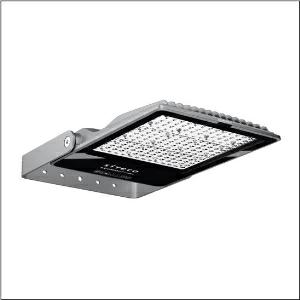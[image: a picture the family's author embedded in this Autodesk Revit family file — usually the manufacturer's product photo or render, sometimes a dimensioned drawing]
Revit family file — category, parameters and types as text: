
# Revit family: sicompact_r__31_midi___pl32_5xa7581d1k23_6975
name_source: partatom
category: Lighting Fixtures
units: mm (PartAtom-declared; Revit-internal decimal feet)

## family parameters
Cut with Voids When Loaded = No
Host = Face
Light Source = No
Part Type = Normal
Room Calculation Point = No
Round Connector Dimension = Use Diameter
Shared = No

## types (1)
- SiCompact® 31 midi  PL32 (1 x LED, 27000 lm, 171 W, 3000K)
    Apparent Load = 171 VA
    CIE Flux Codes = 32 69 98 100 100
    Color Rendering = 70
    Color Temperature = 3000K
    Default Elevation = 1800 mm
    Description = SiCompact® 31 midi, floodlight, primary light control with lens, of plastic, of toughened safety glass, transparent, light distribution: PL32, light emission: direct distribution, primary light characteristic: asymmetric, installation type: surface-mounted, LED, High Power LED, rated luminous flux: 27.000lm, luminous efficacy: 158lm/W, light colour: 730, colour temperature: 3000K, control gear: ECG, with cable, 3x 1.5mm², mains connection: 220..240V, AC, 50/60Hz, connection cable pre-assembled, cable length: 2m, rated input power: 171W, of diecast aluminium, specular, metallic grey (RAL 9006), length: 560mm, width: 330mm, height: 62mm, bracket, of sheet steel, coated, metallic grey (RAL 9006), ON/OFF, protection rating (complete): IP66, insulation class (complete): insulation class I (protective earthing), certification: CE, ENEC, impact resistance: IK08, permissible operating ambient temperature: -40..+45°C, packaging unit: 1 piece

Light Distribution: PL32
    Height = 62 mm  [stored 0.203412 ft]
    Lamp = 1 x LED
    Lamp Light Flux = 27000 lm
    Lamp Power = 171 W
    Lamp count = 1
    Length = 560 mm
    Luminous efficacy = 158 lm/W
    Manufacturer = Siteco
    ModVariant = No
    Model = 5XA7581D1K23
    Mounting Place = Wall
    Mounting Type = Surface mounted
    Number of Poles = 1
    OnlyDefault = Yes
    Power Factor = 1
    Product Name = SiCompact® 31 midi | PL32
    Product group = floodlight | wall mounted
    ProductGroupID = 2001
    Protection Class = Protection class I
    Protection Degree = IP 66
    RLX_Detail_Level = 1
    RLX_Emergency_Light_Flux = 0 lm
    RLX_Emergency_Type = 0
    RLX_Emergency_Type_DB = No
    RlxData = <blob elided: 97637 chars, md5=9ae30cb6>
    Socket = socket
    Standby Power = 0 W
    System Light Flux = 27000 lm
    System Power = 171 W
    Type Comments = Product without accessories
    Type Image = l_1006415.jpg
    URL = http://relux.com
    VarID = ---
    Voltage = 0 V
    Weight = 0.00 kg
    Width = 333 mm

note: [stored X ft] marks values corroborated as IEEE doubles in the binary element streams (Revit-internal decimal feet)

## geometry (parser evidence)
native form markers: Blend x4, Sweep x12
no freeform markers — native parametric forms only
